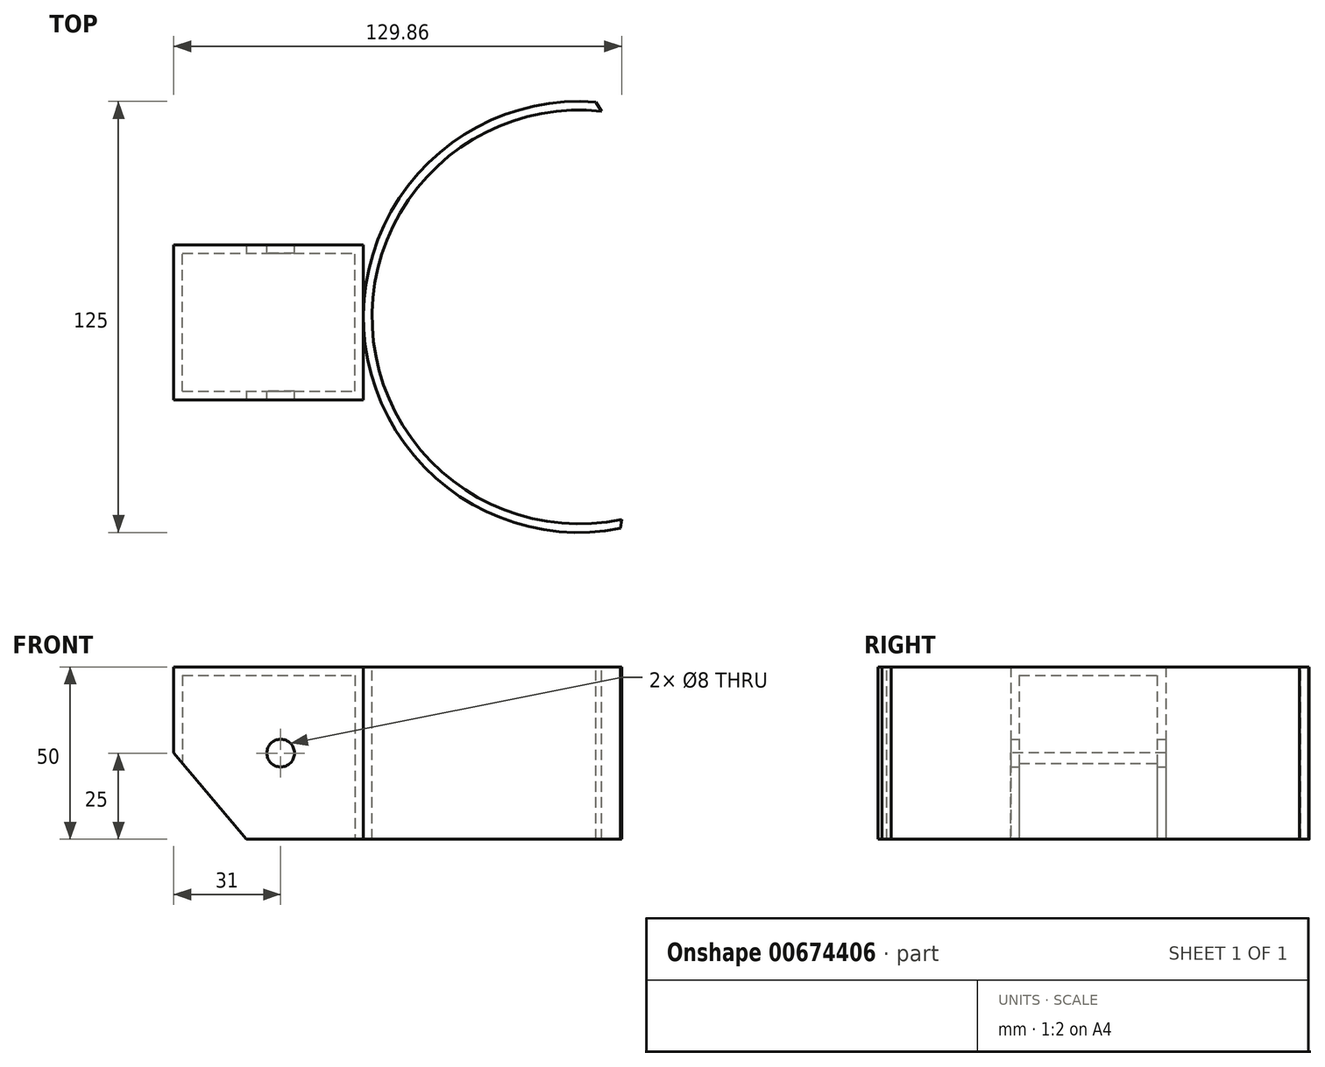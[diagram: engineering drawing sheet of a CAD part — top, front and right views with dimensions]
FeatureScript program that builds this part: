
annotation { "Feature Type Name" : "Feature", "Feature Type Description" : "" }
export const myFeature = defineFeature(function(context is Context, id is Id, definition is map)
    precondition{}
    {
        {
            var Q0;
            Q0=qCreatedBy(makeId("Top.planeOp"),FACE);
            var sketch = newSketch(context, id + "F0", { "sketchPlane" : qUnion([Q0])});
            skLineSegment(sketch, "E0.bottom", {"start": v(-27.5, -22.5) * mm, "end": v(27.5, -22.5) * mm});
            skLineSegment(sketch, "E0.top", {"start": v(-27.5, 22.5) * mm, "end": v(27.5, 22.5) * mm});
            skLineSegment(sketch, "E0.left", {"start": v(-27.5, -22.5) * mm, "end": v(-27.5, 22.5) * mm});
            skLineSegment(sketch, "E0.right", {"start": v(27.5, -22.5) * mm, "end": v(27.5, 22.5) * mm});
            skSolve(sketch);
        }
        {
            var Q0;
            Q0=makeQuery(id+"F0.imprint","IMPRINT",FACE,{"disambiguationData":[TD([[makeQuery(id+"F0.imprint","IMPRINT",EDGE,{"derivedFrom":sQuery(id+"F0.wireOp",EDGE,"E0.bottom")}),1.0]])]});
            extrude(context, id + "F1", {"entities" : qUnion([Q0]), "depth" : 50 * mm, "offsetDistance" : 25 * mm});
        }
        {
            var Q0;
            Q0=makeQuery(id+"F1.opExtrude","CAP_FACE",FACE,{"disambiguationData":[OSD([sQuery(id+"F0.wireOp",EDGE,"E0.bottom"),sQuery(id+"F0.wireOp",EDGE,"E0.top"),sQuery(id+"F0.wireOp",EDGE,"E0.left"),sQuery(id+"F0.wireOp",EDGE,"E0.right")])],"isStart":true});
            shell(context, id + "F2", {"entities" : qUnion([Q0]), "thickness" : 2.5 * mm});
        }
        {
            var Q0;
            Q0=makeQuery(id+"F1.opExtrude","SWEPT_FACE",FACE,{"disambiguationData":[OSD([sQuery(id+"F0.wireOp",EDGE,"E0.top")])]});
            var sketch = newSketch(context, id + "F3", { "sketchPlane" : qUnion([Q0])});
            skCircle(sketch, "E1", {"center": v(-3.5, 25) * mm, "radius": 4 * mm});
            skSolve(sketch);
        }
        {
            var Q0;
            Q0=makeQuery(id+"F3.imprint","IMPRINT",FACE,{"disambiguationData":[TD([[makeQuery(id+"F3.imprint","IMPRINT",EDGE,{"derivedFrom":sQuery(id+"F3.wireOp",EDGE,"E1")}),1.0]])]});
            extrude(context, id + "F4", {"entities" : qUnion([Q0]), "operationType" : NewBodyOperationType.REMOVE, "endBound" : BoundingType.THROUGH_ALL, "oppositeDirection" : true, "depth" : 25 * mm, "offsetDistance" : 25 * mm});
        }
        {
            var Q0;
            Q0=makeQuery(id+"F1.opExtrude","CAP_FACE",FACE,{"disambiguationData":[OSD([sQuery(id+"F0.wireOp",EDGE,"E0.bottom"),sQuery(id+"F0.wireOp",EDGE,"E0.top"),sQuery(id+"F0.wireOp",EDGE,"E0.left"),sQuery(id+"F0.wireOp",EDGE,"E0.right")])],"isStart":false});
            var sketch = newSketch(context, id + "F5", { "sketchPlane" : qUnion([Q0])});
            skArc(sketch, "E2", {"start": v(96.54, 61.2) * mm, "mid": v(30.07, -1.38) * mm, "end": v(102.36, -57.15) * mm});
            skArc(sketch, "E3", {"start": v(94.84, 63.88) * mm, "mid": v(27.6, -2.08) * mm, "end": v(102.06, -59.76) * mm});
            skLineSegment(sketch, "E4", {"start": v(102.06, -59.76) * mm, "end": v(102.36, -57.15) * mm});
            skLineSegment(sketch, "E5", {"start": v(94.84, 63.88) * mm, "end": v(96.54, 61.2) * mm});
            skSolve(sketch);
        }
        {
            var Q0;
            Q0=makeQuery(id+"F5.imprint","IMPRINT",FACE,{"disambiguationData":[TD([[makeQuery(id+"F5.imprint","IMPRINT",EDGE,{"derivedFrom":sQuery(id+"F5.wireOp",EDGE,"E2")}),-1.0]])]});
            extrude(context, id + "F6", {"entities" : qUnion([Q0]), "operationType" : NewBodyOperationType.ADD, "oppositeDirection" : true, "depth" : 50 * mm, "offsetDistance" : 25 * mm});
        }
        {
            var Q0;
            Q0=makeQuery(id+"F1.opExtrude","SWEPT_FACE",FACE,{"disambiguationData":[OSD([sQuery(id+"F0.wireOp",EDGE,"E0.bottom")])]});
            var sketch = newSketch(context, id + "F7", { "sketchPlane" : qUnion([Q0])});
            skLineSegment(sketch, "E6", {"start": v(-27.5, 25.03) * mm, "end": v(-27.5, 0) * mm});
            skLineSegment(sketch, "E7", {"start": v(-27.5, 0) * mm, "end": v(-6.5, 0) * mm});
            skLineSegment(sketch, "E8", {"start": v(-6.5, 0) * mm, "end": v(-27.5, 25.03) * mm});
            skSolve(sketch);
        }
        {
            var Q0;
            Q0=makeQuery(id+"F7.imprint","IMPRINT",FACE,{"disambiguationData":[TD([[makeQuery(id+"F7.imprint","IMPRINT",EDGE,{"derivedFrom":sQuery(id+"F7.wireOp",EDGE,"E6")}),1.0]])]});
            extrude(context, id + "F8", {"entities" : qUnion([Q0]), "operationType" : NewBodyOperationType.REMOVE, "endBound" : BoundingType.THROUGH_ALL, "oppositeDirection" : true, "depth" : 25 * mm, "offsetDistance" : 25 * mm});
        }
    });
